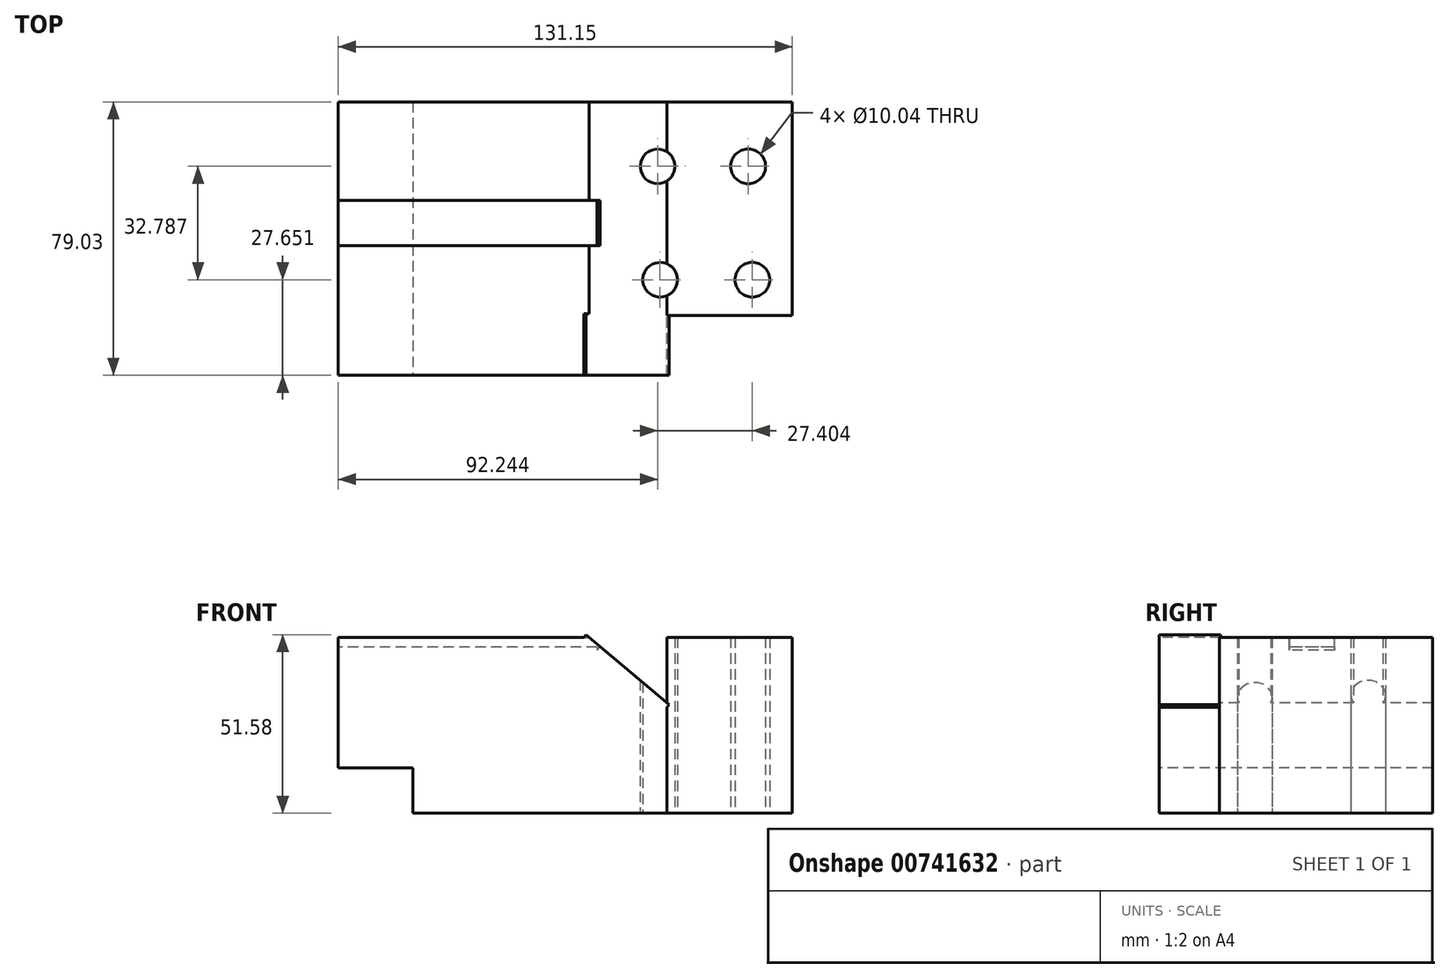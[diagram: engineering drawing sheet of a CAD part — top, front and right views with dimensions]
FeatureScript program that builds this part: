
annotation { "Feature Type Name" : "Feature", "Feature Type Description" : "" }
export const myFeature = defineFeature(function(context is Context, id is Id, definition is map)
    precondition{}
    {
        {
            var Q0;
            Q0=qCreatedBy(makeId("Top.planeOp"),FACE);
            var sketch = newSketch(context, id + "F0", { "sketchPlane" : qUnion([Q0])});
            skLineSegment(sketch, "E0.bottom", {"start": v(-59.09, -37.56) * mm, "end": v(72.06, -37.56) * mm});
            skLineSegment(sketch, "E0.top", {"start": v(-59.09, 41.47) * mm, "end": v(72.06, 41.47) * mm});
            skLineSegment(sketch, "E0.left", {"start": v(-59.09, -37.56) * mm, "end": v(-59.09, 41.47) * mm});
            skLineSegment(sketch, "E0.right", {"start": v(72.06, -37.56) * mm, "end": v(72.06, 41.47) * mm});
            skLineSegment(sketch, "E1", {"start": v(72.06, -20.19) * mm, "end": v(35.85, -20.19) * mm});
            skLineSegment(sketch, "E2", {"start": v(35.85, -20.19) * mm, "end": v(35.85, -37.56) * mm});
            skCircle(sketch, "E3", {"center": v(33.88, -9.9) * mm, "radius": 5.02 * mm});
            skCircle(sketch, "E4", {"center": v(60.56, -9.9) * mm, "radius": 5.02 * mm});
            skCircle(sketch, "E5", {"center": v(33.15, 22.88) * mm, "radius": 5.02 * mm});
            skCircle(sketch, "E6", {"center": v(59.35, 22.88) * mm, "radius": 5.02 * mm});
            skSolve(sketch);
        }
        {
            var Q0;
            Q0 = qSketchRegion(id + "F0", true);
            extrude(context, id + "F1", {"entities" : qUnion([Q0]), "depth" : 50.8 * mm, "offsetDistance" : 25.4 * mm});
        }
        {
            var Q0;
            Q0=makeQuery(id+"F1.opExtrude","CAP_FACE",FACE,{"disambiguationData":[OSD([sQuery(id+"F0.wireOp",EDGE,"E0.bottom"),sQuery(id+"F0.wireOp",EDGE,"E0.top"),sQuery(id+"F0.wireOp",EDGE,"E0.left"),sQuery(id+"F0.wireOp",EDGE,"E0.right"),sQuery(id+"F0.wireOp",EDGE,"E3"),sQuery(id+"F0.wireOp",EDGE,"E4"),sQuery(id+"F0.wireOp",EDGE,"E5"),sQuery(id+"F0.wireOp",EDGE,"E6")])],"isStart":false});
            var sketch = newSketch(context, id + "F2", { "sketchPlane" : qUnion([Q0])});
            skLineSegment(sketch, "E7", {"start": v(35.85, -37.56) * mm, "end": v(72.06, -37.56) * mm});
            skLineSegment(sketch, "E8", {"start": v(72.06, -20.19) * mm, "end": v(35.85, -20.19) * mm});
            skLineSegment(sketch, "E9", {"start": v(35.85, -37.56) * mm, "end": v(35.85, -20.19) * mm});
            skSolve(sketch);
        }
        {
            var Q0;
            {var subQ0=sQuery(id+"F2.wireOp",EDGE,"E7");Q0=makeQuery(id+"F2.imprint","IMPRINT",FACE,{"disambiguationData":[TD([[makeQuery(id+"F2.imprint","IMPRINT",EDGE,{"derivedFrom":subQ0}),1.0]])]});}
            extrude(context, id + "F3", {"entities" : qUnion([Q0]), "operationType" : NewBodyOperationType.REMOVE, "oppositeDirection" : true, "depth" : 50.8 * mm, "offsetDistance" : 25.4 * mm});
        }
        {
            var Q0;
            Q0=makeQuery(id+"F1.opExtrude","SWEPT_FACE",FACE,{"disambiguationData":[OSD([sQuery(id+"F0.wireOp",EDGE,"E0.bottom")])]});
            var sketch = newSketch(context, id + "F4", { "sketchPlane" : qUnion([Q0])});
            skLineSegment(sketch, "E10", {"start": v(72.06, 0) * mm, "end": v(11.87, 50.8) * mm});
            skSolve(sketch);
        }
        {
            var Q0;
            Q0 = qSketchRegion(id + "F4", true);
            var Q1;
            {var subQ0=sQuery(id+"F4.wireOp",EDGE,"E10");var subQ1=sQuery(id+"F0.wireOp",EDGE,"E0.bottom");var subQ2=makeQuery(id+"F1.opExtrude","CAP_EDGE",EDGE,{"disambiguationData":[OSD([subQ1])],"isStart":false});var subQ3=makeQuery(id+"F4.imprint","INTERSECT",VERTEX,{"derivedFrom":[subQ2,subQ0]});Q1=makeQuery(id+"F4.imprint","IMPRINT",FACE,{"disambiguationData":[TD([[makeQuery(id+"F4.imprint","IMPRINT",EDGE,{"disambiguationData":[TD([[subQ3,1.0]])],"derivedFrom":subQ0}),-1.0]])]});}
            extrude(context, id + "F5", {"entities" : qUnion([Q0, Q1]), "operationType" : NewBodyOperationType.ADD, "depth" : 50.8 * mm, "offsetDistance" : 25.4 * mm});
        }
        {
            var Q0;
            {var subQ1=sQuery(id+"F0.wireOp",EDGE,"E0.top");Q0=makeQuery(id+"F0.imprint","IMPRINT",FACE,{"disambiguationData":[TD([[makeQuery(id+"F0.imprint","IMPRINT",EDGE,{"derivedFrom":subQ1}),-1.0]])]});}
            var sketch = newSketch(context, id + "F6", { "sketchPlane" : qUnion([Q0])});
            skLineSegment(sketch, "E11", {"start": v(-60.1, 25.76) * mm, "end": v(-25.76, 25.76) * mm});
            skLineSegment(sketch, "E12", {"start": v(-25.76, 25.76) * mm, "end": v(-25.76, 41.6) * mm});
            skLineSegment(sketch, "E13", {"start": v(-25.76, 41.6) * mm, "end": v(-59.05, 41.6) * mm});
            skLineSegment(sketch, "E14", {"start": v(-59.05, 41.6) * mm, "end": v(-60.1, 25.76) * mm});
            skSolve(sketch);
        }
        {
            var Q0;
            {var subQ0=sQuery(id+"F6.wireOp",EDGE,"E14");var subQ1=sQuery(id+"F6.wireOp",EDGE,"E11");var subQ2=makeQuery(id+"F6.imprint","INTERSECT",VERTEX,{"derivedFrom":[subQ1,subQ0]});Q0=makeQuery(id+"F6.imprint","IMPRINT",FACE,{"disambiguationData":[TD([[makeQuery(id+"F6.imprint","IMPRINT",EDGE,{"disambiguationData":[TD([[subQ2,-1.0]])],"derivedFrom":subQ1}),1.0]])]});}
            var Q1;
            {var subQ0=sQuery(id+"F6.wireOp",EDGE,"E13");Q1=makeQuery(id+"F6.imprint","IMPRINT",FACE,{"disambiguationData":[TD([[makeQuery(id+"F6.imprint","IMPRINT",EDGE,{"derivedFrom":subQ0}),1.0]])]});}
            var Q2;
            {var subQ0=sQuery(id+"F6.wireOp",EDGE,"E12");var subQ5=sQuery(id+"F6.wireOp",EDGE,"E11");var subQ6=makeQuery(id+"F6.imprint","INTERSECT",VERTEX,{"derivedFrom":[subQ5,subQ0]});Q2=makeQuery(id+"F6.imprint","IMPRINT",FACE,{"disambiguationData":[TD([[makeQuery(id+"F6.imprint","IMPRINT",EDGE,{"disambiguationData":[TD([[subQ6,1.0]])],"derivedFrom":subQ5}),1.0]])]});}
            extrude(context, id + "F7", {"entities" : qUnion([Q0, Q1, Q2]), "operationType" : NewBodyOperationType.REMOVE, "oppositeDirection" : true, "depth" : 50.8 * mm, "offsetDistance" : 25.4 * mm});
        }
        {
            var Q0;
            Q0=makeQuery(id+"F5.opExtrude","CAP_FACE",FACE,{"disambiguationData":[OSD([sQuery(id+"F0.wireOp",EDGE,"E0.bottom"),sQuery(id+"F2.wireOp",EDGE,"E7"),sQuery(id+"F2.wireOp",EDGE,"E9"),sQuery(id+"F4.wireOp",EDGE,"E10")])],"isStart":false});
            extrude(context, id + "F8", {"entities" : qUnion([Q0]), "operationType" : NewBodyOperationType.REMOVE, "oppositeDirection" : true, "depth" : 68.58 * mm, "offsetDistance" : 25.4 * mm});
        }
        {
            var Q0;
            Q0=makeQuery(id+"F8.boolean.opBoolean","COPY",FACE,{"derivedFrom":makeQuery(id+"F8.opExtrude","SWEPT_FACE",FACE,{"disambiguationData":[OSD([sQuery(id+"F4.wireOp",EDGE,"E10")])]})});
            extrude(context, id + "F9", {"entities" : qUnion([Q0]), "operationType" : NewBodyOperationType.ADD, "depth" : 1.02 * mm, "offsetDistance" : 25.4 * mm});
        }
        {
            var Q0;
            Q0=makeQuery(id+"F3.boolean.opBoolean","COPY",FACE,{"derivedFrom":makeQuery(id+"F3.opExtrude","SWEPT_FACE",FACE,{"disambiguationData":[OSD([sQuery(id+"F2.wireOp",EDGE,"E8")])]})});
            var sketch = newSketch(context, id + "F10", { "sketchPlane" : qUnion([Q0])});
            skLineSegment(sketch, "E15", {"start": v(72.06, 0) * mm, "end": v(14.8, 50.77) * mm});
            skSolve(sketch);
        }
        {
            var Q0;
            Q0=makeQuery(id+"F8.boolean.opBoolean","COPY",FACE,{"derivedFrom":makeQuery(id+"F8.opExtrude","CAP_FACE",FACE,{"disambiguationData":[OSD([sQuery(id+"F0.wireOp",EDGE,"E0.bottom"),sQuery(id+"F2.wireOp",EDGE,"E7"),sQuery(id+"F2.wireOp",EDGE,"E9"),sQuery(id+"F4.wireOp",EDGE,"E10")])],"isStart":false})});
            var Q1;
            {var subQ1=sQuery(id+"F2.wireOp",EDGE,"E8");var subQ6=makeQuery(id+"F3.boolean.opBoolean","COPY",EDGE,{"derivedFrom":makeQuery(id+"F3.opExtrude","CAP_EDGE",EDGE,{"disambiguationData":[OSD([subQ1])],"isStart":true})});Q1=makeQuery(id+"F10.imprint","IMPRINT",FACE,{"disambiguationData":[TD([[makeQuery(id+"F10.imprint","IMPRINT",EDGE,{"derivedFrom":subQ6}),1.0]])]});}
            extrude(context, id + "F11", {"entities" : qUnion([Q0, Q1]), "operationType" : NewBodyOperationType.REMOVE, "oppositeDirection" : true, "depth" : 63.5 * mm, "offsetDistance" : 25.4 * mm});
        }
        {
            var Q0;
            {var subQ0=sQuery(id+"F4.wireOp",EDGE,"E10");Q0=makeQuery(id+"F9.boolean.opBoolean","MERGE",FACE,{"derivedFrom":[makeQuery(id+"F1.opExtrude","SWEPT_FACE",FACE,{"disambiguationData":[OSD([sQuery(id+"F0.wireOp",EDGE,"E0.bottom")])]}),makeQuery(id+"F9.opExtrude","SWEPT_FACE",FACE,{"disambiguationData":[OSD([subQ0]),TDD([makeQuery(id+"F5.opExtrude","CAP_EDGE",EDGE,{"disambiguationData":[OSD([subQ0])],"isStart":true})])]})]});}
            var sketch = newSketch(context, id + "F12", { "sketchPlane" : qUnion([Q0])});
            skLineSegment(sketch, "E16", {"start": v(-59.09, 13.1) * mm, "end": v(-37.56, 13.1) * mm});
            skLineSegment(sketch, "E17", {"start": v(-37.56, 13.1) * mm, "end": v(-37.56, 0) * mm});
            skSolve(sketch);
        }
        {
            var Q0;
            {var subQ0=sQuery(id+"F12.wireOp",EDGE,"E16");Q0=makeQuery(id+"F12.imprint","IMPRINT",FACE,{"disambiguationData":[TD([[makeQuery(id+"F12.imprint","IMPRINT",EDGE,{"derivedFrom":subQ0}),-1.0]])]});}
            extrude(context, id + "F13", {"entities" : qUnion([Q0]), "operationType" : NewBodyOperationType.REMOVE, "oppositeDirection" : true, "depth" : 76.2 * mm, "offsetDistance" : 25.4 * mm});
        }
        {
            var Q0;
            Q0=makeQuery(id+"F13.boolean.opBoolean","COPY",FACE,{"derivedFrom":makeQuery(id+"F13.opExtrude","CAP_FACE",FACE,{"disambiguationData":[OSD([sQuery(id+"F0.wireOp",EDGE,"E0.bottom"),sQuery(id+"F0.wireOp",EDGE,"E0.left"),sQuery(id+"F12.wireOp",EDGE,"E16"),sQuery(id+"F12.wireOp",EDGE,"E17")])],"isStart":false})});
            extrude(context, id + "F14", {"entities" : qUnion([Q0]), "operationType" : NewBodyOperationType.REMOVE, "oppositeDirection" : true, "depth" : 25.4 * mm, "offsetDistance" : 25.4 * mm});
        }
        {
            var Q0;
            {var subQ0=sQuery(id+"F0.wireOp",EDGE,"E0.bottom");Q0=makeQuery(id+"F5.boolean.opBoolean","MERGE",FACE,{"derivedFrom":[makeQuery(id+"F1.opExtrude","CAP_FACE",FACE,{"disambiguationData":[OSD([subQ0,sQuery(id+"F0.wireOp",EDGE,"E0.top"),sQuery(id+"F0.wireOp",EDGE,"E0.left"),sQuery(id+"F0.wireOp",EDGE,"E0.right"),sQuery(id+"F0.wireOp",EDGE,"E3"),sQuery(id+"F0.wireOp",EDGE,"E4"),sQuery(id+"F0.wireOp",EDGE,"E5"),sQuery(id+"F0.wireOp",EDGE,"E6")])],"isStart":false}),makeQuery(id+"F5.opExtrude","SWEPT_FACE",FACE,{"disambiguationData":[OSD([subQ0])]})]});}
            var sketch = newSketch(context, id + "F15", { "sketchPlane" : qUnion([Q0])});
            skLineSegment(sketch, "E18", {"start": v(13.44, 0) * mm, "end": v(-59.09, 0) * mm});
            skLineSegment(sketch, "E19", {"start": v(-59.09, 0) * mm, "end": v(-59.09, 13.1) * mm});
            skLineSegment(sketch, "E20", {"start": v(-59.09, 13.1) * mm, "end": v(13.44, 13.1) * mm});
            skLineSegment(sketch, "E21", {"start": v(13.44, 13.1) * mm, "end": v(13.44, 0) * mm});
            skSolve(sketch);
        }
        {
            var Q0;
            Q0=makeQuery(id+"F15.imprint","IMPRINT",FACE,{"disambiguationData":[TD([[makeQuery(id+"F15.imprint","IMPRINT",EDGE,{"derivedFrom":sQuery(id+"F15.wireOp",EDGE,"E18")}),-1.0]])]});
            extrude(context, id + "F16", {"entities" : qUnion([Q0]), "operationType" : NewBodyOperationType.REMOVE, "oppositeDirection" : true, "depth" : 12.7 * mm, "offsetDistance" : 25.4 * mm});
        }
        {
            var Q0;
            {var subQ0=sQuery(id+"F4.wireOp",EDGE,"E10");Q0=makeQuery(id+"F11.boolean.opBoolean","MERGE",FACE,{"derivedFrom":[makeQuery(id+"F9.opExtrude","CAP_FACE",FACE,{"disambiguationData":[OSD([subQ0])],"isStart":false}),makeQuery(id+"F11.opExtrude","SWEPT_FACE",FACE,{"disambiguationData":[OSD([subQ0])]})]});}
            var sketch = newSketch(context, id + "F17", { "sketchPlane" : qUnion([Q0])});
            skLineSegment(sketch, "E22", {"start": v(-22.5, 0) * mm, "end": v(-18.4, 0) * mm});
            skLineSegment(sketch, "E23", {"start": v(-18.4, 0) * mm, "end": v(-18.4, 13.1) * mm});
            skLineSegment(sketch, "E24", {"start": v(-18.4, 13.1) * mm, "end": v(-22.5, 13.1) * mm});
            skSolve(sketch);
        }
        {
            var Q0;
            Q0=makeQuery(id+"F17.imprint","IMPRINT",FACE,{"disambiguationData":[TD([[makeQuery(id+"F17.imprint","IMPRINT",EDGE,{"derivedFrom":sQuery(id+"F17.wireOp",EDGE,"E22")}),1.0]])]});
            extrude(context, id + "F18", {"entities" : qUnion([Q0]), "operationType" : NewBodyOperationType.REMOVE, "oppositeDirection" : true, "depth" : 12.7 * mm, "offsetDistance" : 25.4 * mm});
        }
        {
            var Q0;
            Q0=makeQuery(id+"F16.boolean.opBoolean","COPY",FACE,{"derivedFrom":makeQuery(id+"F16.opExtrude","CAP_FACE",FACE,{"disambiguationData":[OSD([sQuery(id+"F15.wireOp",EDGE,"E18"),sQuery(id+"F15.wireOp",EDGE,"E19"),sQuery(id+"F15.wireOp",EDGE,"E20"),sQuery(id+"F15.wireOp",EDGE,"E21")])],"isStart":false})});
            extrude(context, id + "F19", {"entities" : qUnion([Q0]), "operationType" : NewBodyOperationType.ADD, "depth" : 6.35 * mm, "offsetDistance" : 25.4 * mm});
        }
        {
            var Q0;
            Q0=makeQuery(id+"F19.opExtrude","CAP_FACE",FACE,{"disambiguationData":[OSD([sQuery(id+"F15.wireOp",EDGE,"E18"),sQuery(id+"F15.wireOp",EDGE,"E19"),sQuery(id+"F15.wireOp",EDGE,"E20"),sQuery(id+"F15.wireOp",EDGE,"E21")])],"isStart":false});
            extrude(context, id + "F20", {"entities" : qUnion([Q0]), "operationType" : NewBodyOperationType.ADD, "depth" : 5.08 * mm, "offsetDistance" : 25.4 * mm});
        }
        {
            var Q0;
            Q0=makeQuery(id+"F20.opExtrude","SWEPT_FACE",FACE,{"disambiguationData":[OSD([sQuery(id+"F15.wireOp",EDGE,"E21"),sQuery(id+"F17.wireOp",EDGE,"E23")])]});
            extrude(context, id + "F21", {"entities" : qUnion([Q0]), "operationType" : NewBodyOperationType.ADD, "depth" : 2.26 * mm, "offsetDistance" : 25.4 * mm});
        }
        {
            var Q0;
            {var subQ0=sQuery(id+"F17.wireOp",EDGE,"E23");var subQ1=sQuery(id+"F15.wireOp",EDGE,"E21");Q0=makeQuery(id+"F21.boolean.opBoolean","MERGE",FACE,{"derivedFrom":[makeQuery(id+"F20.opExtrude","CAP_FACE",FACE,{"disambiguationData":[OSD([sQuery(id+"F15.wireOp",EDGE,"E18"),sQuery(id+"F15.wireOp",EDGE,"E19"),sQuery(id+"F15.wireOp",EDGE,"E20"),subQ1])],"isStart":false}),makeQuery(id+"F21.opExtrude","SWEPT_FACE",FACE,{"disambiguationData":[OSD([subQ1,subQ0]),TDD([makeQuery(id+"F20.opExtrude","CAP_EDGE",EDGE,{"disambiguationData":[OSD([subQ1,subQ0])],"isStart":false})])]})]});}
            extrude(context, id + "F22", {"entities" : qUnion([Q0]), "operationType" : NewBodyOperationType.REMOVE, "oppositeDirection" : true, "depth" : 2.03 * mm, "offsetDistance" : 25.4 * mm});
        }
        {
            var Q0;
            Q0=makeQuery(id+"F22.boolean.opBoolean","COPY",FACE,{"derivedFrom":makeQuery(id+"F22.opExtrude","CAP_FACE",FACE,{"disambiguationData":[OSD([sQuery(id+"F15.wireOp",EDGE,"E18"),sQuery(id+"F15.wireOp",EDGE,"E19"),sQuery(id+"F15.wireOp",EDGE,"E20"),sQuery(id+"F15.wireOp",EDGE,"E21"),sQuery(id+"F17.wireOp",EDGE,"E23")])],"isStart":false})});
            extrude(context, id + "F23", {"entities" : qUnion([Q0]), "operationType" : NewBodyOperationType.ADD, "depth" : 1.52 * mm, "offsetDistance" : 25.4 * mm});
        }
        {
            var Q0;
            Q0=makeQuery(id+"F23.opExtrude","CAP_FACE",FACE,{"disambiguationData":[OSD([sQuery(id+"F15.wireOp",EDGE,"E18"),sQuery(id+"F15.wireOp",EDGE,"E19"),sQuery(id+"F15.wireOp",EDGE,"E20"),sQuery(id+"F15.wireOp",EDGE,"E21"),sQuery(id+"F17.wireOp",EDGE,"E23")])],"isStart":false});
            extrude(context, id + "F24", {"entities" : qUnion([Q0]), "operationType" : NewBodyOperationType.REMOVE, "oppositeDirection" : true, "depth" : 1.02 * mm, "offsetDistance" : 25.4 * mm});
        }
    });
